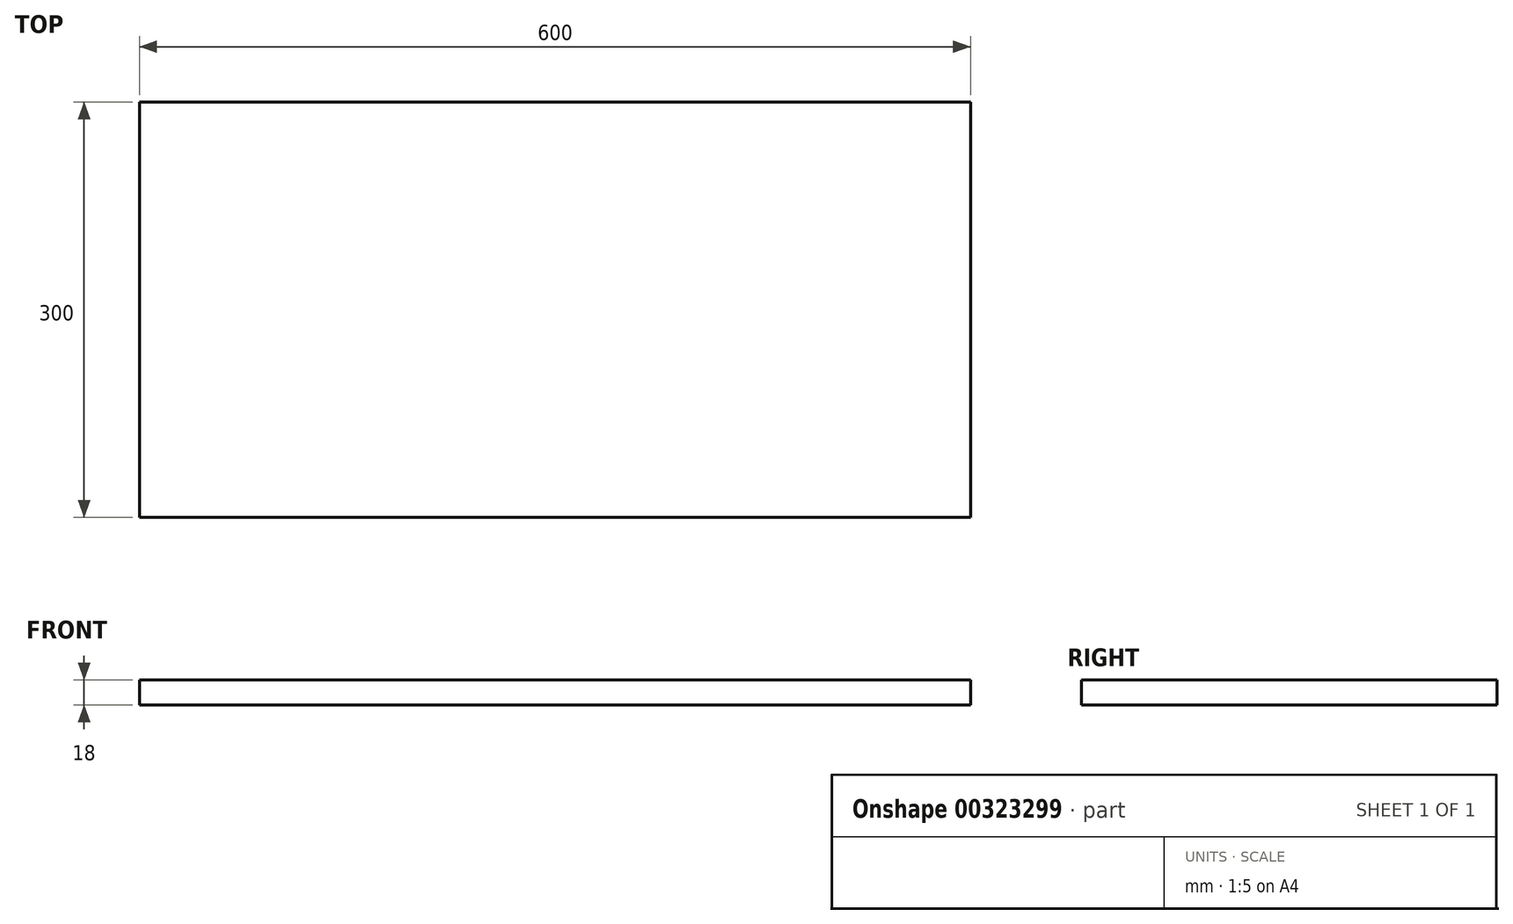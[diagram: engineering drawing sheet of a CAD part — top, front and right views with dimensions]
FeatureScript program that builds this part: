
annotation { "Feature Type Name" : "Feature", "Feature Type Description" : "" }
export const myFeature = defineFeature(function(context is Context, id is Id, definition is map)
    precondition{}
    {
        {
            var Q0;
            Q0=qCreatedBy(makeId("Top.planeOp"),FACE);
            var sketch = newSketch(context, id + "F0", { "sketchPlane" : qUnion([Q0])});
            skLineSegment(sketch, "E0.bottom", {"start": v(0, 0) * mm, "end": v(600, 0) * mm});
            skLineSegment(sketch, "E0.top", {"start": v(0, 300) * mm, "end": v(600, 300) * mm});
            skLineSegment(sketch, "E0.left", {"start": v(0, 0) * mm, "end": v(0, 300) * mm});
            skLineSegment(sketch, "E0.right", {"start": v(600, 0) * mm, "end": v(600, 300) * mm});
            skSolve(sketch);
        }
        {
            var Q0;
            Q0 = qSketchRegion(id + "F0", true);
            extrude(context, id + "F1", {"entities" : qUnion([Q0]), "depth" : 18 * mm, "offsetDistance" : 25 * mm});
        }
    });
